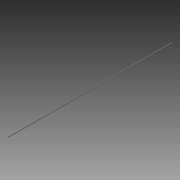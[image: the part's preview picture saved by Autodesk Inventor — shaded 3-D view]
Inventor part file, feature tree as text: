
AUTODESK INVENTOR PART (.ipt)
format: ipt  version: 2013 (Build 170138000, 138)  size: 84,992 bytes
history: native  units: in
note: dims shown in document units (in); Inventor stores cm internally (conversion verified against a paired STEP export)
features: other x2, plane x1, extrude x1, sketch x1
ambient origin geometry x8: Origin, YZ Plane, XZ Plane, XY Plane, X Axis, Y Axis, Z Axis, Center Point
feature tree (5):
  other  "Table"
  other  "vee-track-01"
  plane  "Work Plane1"
  extrude  "Extrusion1"  [1 undecoded]
  sketch  "Sketch1"  dims[d1=0.0in]
note: 1 required parameter value undecoded (feature->parameter linkage not recoverable at this tier; creation-order binding heuristic only, values carry confidence <= 0.55)
